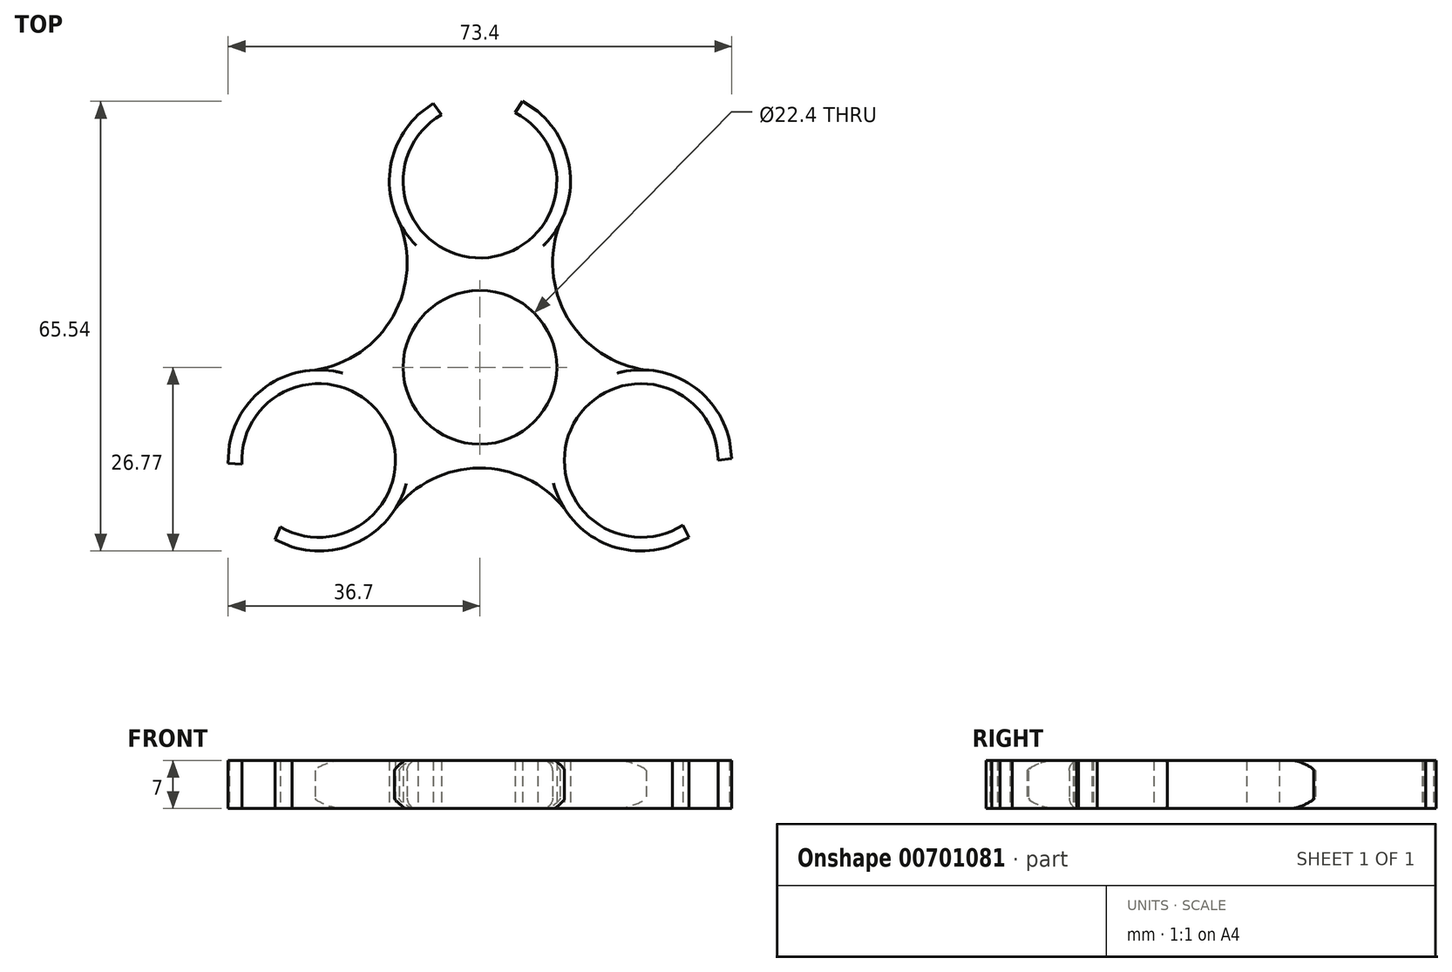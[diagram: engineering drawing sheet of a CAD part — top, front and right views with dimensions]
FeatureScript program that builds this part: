
annotation { "Feature Type Name" : "Feature", "Feature Type Description" : "" }
export const myFeature = defineFeature(function(context is Context, id is Id, definition is map)
    precondition{}
    {
        {
            var Q0;
            Q0=qCreatedBy(makeId("Top.planeOp"),FACE);
            var sketch = newSketch(context, id + "F0", { "sketchPlane" : qUnion([Q0])});
            skCircle(sketch, "E0", {"center": v(0, 0) * mm, "radius": 11.2 * mm});
            skArc(sketch, "E1", {"start": v(-6.82, 38.44) * mm, "mid": v(0.34, 13.94) * mm, "end": v(6.24, 38.77) * mm});
            skArc(sketch, "E2", {"start": v(-5.6, 36.83) * mm, "mid": v(0.28, 15.94) * mm, "end": v(5.12, 37.1) * mm});
            skArc(sketch, "E3.1.0", {"start": v(-29.1, -23.28) * mm, "mid": v(-13.95, -7.73) * mm, "end": v(-34.7, -14.12) * mm});
            skArc(sketch, "E3.1.1", {"start": v(-29.88, -25.13) * mm, "mid": v(-12.24, -6.68) * mm, "end": v(-36.7, -13.98) * mm});
            skArc(sketch, "E3.2.0", {"start": v(34.7, -13.56) * mm, "mid": v(13.67, -8.22) * mm, "end": v(29.57, -22.98) * mm});
            skArc(sketch, "E3.2.1", {"start": v(36.7, -13.31) * mm, "mid": v(11.9, -7.26) * mm, "end": v(30.46, -24.8) * mm});
            skLineSegment(sketch, "E4", {"start": v(6.24, 38.77) * mm, "end": v(8.44, 37.3) * mm});
            skLineSegment(sketch, "E5.1.0", {"start": v(-36.7, -13.98) * mm, "end": v(-36.51, -11.34) * mm});
            skLineSegment(sketch, "E5.2.0", {"start": v(30.46, -24.8) * mm, "end": v(28.08, -25.95) * mm});
            skLineSegment(sketch, "E6", {"start": v(-6.82, 38.44) * mm, "end": v(-9, 36.8) * mm});
            skLineSegment(sketch, "E7.1.0", {"start": v(-29.88, -25.13) * mm, "end": v(-27.36, -26.2) * mm});
            skLineSegment(sketch, "E7.2.0", {"start": v(36.7, -13.31) * mm, "end": v(36.36, -10.6) * mm});
            skArc(sketch, "E8", {"start": v(11.68, 20.99) * mm, "mid": v(12.77, 7.24) * mm, "end": v(24.25, -0.4) * mm});
            skArc(sketch, "E9.1.0", {"start": v(-24.01, -0.38) * mm, "mid": v(-12.66, 7.44) * mm, "end": v(-11.78, 21.2) * mm});
            skArc(sketch, "E9.2.0", {"start": v(12.34, -20.6) * mm, "mid": v(-0.11, -14.68) * mm, "end": v(-12.46, -20.8) * mm});
            skLineSegment(sketch, "E10", {"start": v(8.44, 37.3) * mm, "end": v(10.63, 30.66) * mm});
            skLineSegment(sketch, "E11", {"start": v(10.63, 30.66) * mm, "end": v(12.83, 24.03) * mm});
            skLineSegment(sketch, "E12", {"start": v(12.83, 24.03) * mm, "end": v(7.84, 19.14) * mm});
            skLineSegment(sketch, "E13", {"start": v(7.84, 19.14) * mm, "end": v(2.85, 14.25) * mm});
            skLineSegment(sketch, "E14", {"start": v(2.85, 14.25) * mm, "end": v(-3.74, 16.58) * mm});
            skLineSegment(sketch, "E15", {"start": v(-3.74, 16.58) * mm, "end": v(-10.32, 18.91) * mm});
            skLineSegment(sketch, "E16", {"start": v(-10.32, 18.91) * mm, "end": v(-10.91, 24.03) * mm});
            skLineSegment(sketch, "E17", {"start": v(-10.91, 24.03) * mm, "end": v(-13.1, 28.7) * mm});
            skLineSegment(sketch, "E18", {"start": v(-13.1, 28.7) * mm, "end": v(-8.74, 34.14) * mm});
            skLineSegment(sketch, "E19", {"start": v(-8.74, 34.14) * mm, "end": v(-6.82, 38.44) * mm});
            skLineSegment(sketch, "E20.1.0", {"start": v(-25.2, -24.64) * mm, "end": v(-29.88, -25.13) * mm});
            skLineSegment(sketch, "E20.1.1", {"start": v(-18.3, -25.7) * mm, "end": v(-25.2, -24.64) * mm});
            skLineSegment(sketch, "E20.1.2", {"start": v(-15.35, -21.47) * mm, "end": v(-18.3, -25.7) * mm});
            skLineSegment(sketch, "E20.1.3", {"start": v(-11.22, -18.4) * mm, "end": v(-15.35, -21.47) * mm});
            skLineSegment(sketch, "E20.1.4", {"start": v(-12.5, -11.53) * mm, "end": v(-11.22, -18.4) * mm});
            skLineSegment(sketch, "E20.1.5", {"start": v(-13.77, -4.66) * mm, "end": v(-12.5, -11.53) * mm});
            skLineSegment(sketch, "E20.1.6", {"start": v(-20.5, -2.78) * mm, "end": v(-13.77, -4.66) * mm});
            skLineSegment(sketch, "E20.1.7", {"start": v(-27.22, -0.9) * mm, "end": v(-20.5, -2.78) * mm});
            skLineSegment(sketch, "E20.1.8", {"start": v(-31.87, -6.12) * mm, "end": v(-27.22, -0.9) * mm});
            skLineSegment(sketch, "E20.1.9", {"start": v(-36.51, -11.34) * mm, "end": v(-31.87, -6.12) * mm});
            skLineSegment(sketch, "E20.2.0", {"start": v(33.94, -9.5) * mm, "end": v(36.7, -13.31) * mm});
            skLineSegment(sketch, "E20.2.1", {"start": v(31.4, -3) * mm, "end": v(33.94, -9.5) * mm});
            skLineSegment(sketch, "E20.2.2", {"start": v(26.27, -2.56) * mm, "end": v(31.4, -3) * mm});
            skLineSegment(sketch, "E20.2.3", {"start": v(21.54, -0.52) * mm, "end": v(26.27, -2.56) * mm});
            skLineSegment(sketch, "E20.2.4", {"start": v(16.23, -5.06) * mm, "end": v(21.54, -0.52) * mm});
            skLineSegment(sketch, "E20.2.5", {"start": v(10.92, -9.6) * mm, "end": v(16.23, -5.06) * mm});
            skLineSegment(sketch, "E20.2.6", {"start": v(12.66, -16.36) * mm, "end": v(10.92, -9.6) * mm});
            skLineSegment(sketch, "E20.2.7", {"start": v(14.4, -23.12) * mm, "end": v(12.66, -16.36) * mm});
            skLineSegment(sketch, "E20.2.8", {"start": v(21.24, -24.54) * mm, "end": v(14.4, -23.12) * mm});
            skLineSegment(sketch, "E20.2.9", {"start": v(28.08, -25.95) * mm, "end": v(21.24, -24.54) * mm});
            skLineSegment(sketch, "E21", {"start": v(-6.82, 38.44) * mm, "end": v(-5.6, 36.83) * mm});
            skLineSegment(sketch, "E22", {"start": v(6.24, 38.77) * mm, "end": v(5.12, 37.1) * mm});
            skLineSegment(sketch, "E23.1.0", {"start": v(-29.88, -25.13) * mm, "end": v(-29.1, -23.28) * mm});
            skLineSegment(sketch, "E23.1.1", {"start": v(-36.7, -13.98) * mm, "end": v(-34.7, -14.12) * mm});
            skLineSegment(sketch, "E23.2.0", {"start": v(36.7, -13.31) * mm, "end": v(34.7, -13.56) * mm});
            skLineSegment(sketch, "E23.2.1", {"start": v(30.46, -24.8) * mm, "end": v(29.57, -22.98) * mm});
            skSolve(sketch);
        }
        {
            var Q0;
            {var subQ0=sQuery(id+"F0.wireOp",EDGE,"E13");Q0=makeQuery(id+"F0.imprint","IMPRINT",FACE,{"disambiguationData":[TD([[makeQuery(id+"F0.imprint","IMPRINT",EDGE,{"derivedFrom":subQ0}),-1.0]])]});}
            var Q1;
            {var subQ0=sQuery(id+"F0.wireOp",EDGE,"E11");Q1=makeQuery(id+"F0.imprint","IMPRINT",FACE,{"disambiguationData":[TD([[makeQuery(id+"F0.imprint","IMPRINT",EDGE,{"derivedFrom":subQ0}),-1.0]])]});}
            var Q2;
            Q2=makeQuery(id+"F0.imprint","IMPRINT",FACE,{"disambiguationData":[TD([[makeQuery(id+"F0.imprint","IMPRINT",EDGE,{"derivedFrom":sQuery(id+"F0.wireOp",EDGE,"E4")}),-1.0]])]});
            var Q3;
            {var subQ0=sQuery(id+"F0.wireOp",EDGE,"E10");Q3=makeQuery(id+"F0.imprint","IMPRINT",FACE,{"disambiguationData":[TD([[makeQuery(id+"F0.imprint","IMPRINT",EDGE,{"derivedFrom":subQ0}),1.0]])]});}
            var Q4;
            {var subQ3=sQuery(id+"F0.wireOp",EDGE,"E12");Q4=makeQuery(id+"F0.imprint","IMPRINT",FACE,{"disambiguationData":[TD([[makeQuery(id+"F0.imprint","IMPRINT",EDGE,{"derivedFrom":subQ3}),1.0]])]});}
            var Q5;
            {var subQ0=sQuery(id+"F0.wireOp",EDGE,"E14");Q5=makeQuery(id+"F0.imprint","IMPRINT",FACE,{"disambiguationData":[TD([[makeQuery(id+"F0.imprint","IMPRINT",EDGE,{"derivedFrom":subQ0}),1.0]])]});}
            var Q6;
            {var subQ0=sQuery(id+"F0.wireOp",EDGE,"E6");Q6=makeQuery(id+"F0.imprint","IMPRINT",FACE,{"disambiguationData":[TD([[makeQuery(id+"F0.imprint","IMPRINT",EDGE,{"derivedFrom":subQ0}),1.0]])]});}
            var Q7;
            {var subQ0=sQuery(id+"F0.wireOp",EDGE,"E15");Q7=makeQuery(id+"F0.imprint","IMPRINT",FACE,{"disambiguationData":[TD([[makeQuery(id+"F0.imprint","IMPRINT",EDGE,{"derivedFrom":subQ0}),-1.0]])]});}
            var Q8;
            {var subQ3=sQuery(id+"F0.wireOp",EDGE,"E16");Q8=makeQuery(id+"F0.imprint","IMPRINT",FACE,{"disambiguationData":[TD([[makeQuery(id+"F0.imprint","IMPRINT",EDGE,{"derivedFrom":subQ3}),1.0]])]});}
            var Q9;
            Q9=makeQuery(id+"F0.imprint","IMPRINT",FACE,{"disambiguationData":[TD([[makeQuery(id+"F0.imprint","IMPRINT",EDGE,{"derivedFrom":sQuery(id+"F0.wireOp",EDGE,"E0")}),-1.0]])]});
            var Q10;
            {var subQ2=sQuery(id+"F0.wireOp",EDGE,"E20.1.6");Q10=makeQuery(id+"F0.imprint","IMPRINT",FACE,{"disambiguationData":[TD([[makeQuery(id+"F0.imprint","IMPRINT",EDGE,{"derivedFrom":subQ2}),1.0]])]});}
            var Q11;
            {var subQ0=sQuery(id+"F0.wireOp",EDGE,"E20.1.4");Q11=makeQuery(id+"F0.imprint","IMPRINT",FACE,{"disambiguationData":[TD([[makeQuery(id+"F0.imprint","IMPRINT",EDGE,{"derivedFrom":subQ0}),1.0]])]});}
            var Q12;
            {var subQ0=sQuery(id+"F0.wireOp",EDGE,"E20.1.5");Q12=makeQuery(id+"F0.imprint","IMPRINT",FACE,{"disambiguationData":[TD([[makeQuery(id+"F0.imprint","IMPRINT",EDGE,{"derivedFrom":subQ0}),-1.0]])]});}
            var Q13;
            {var subQ0=sQuery(id+"F0.wireOp",EDGE,"E20.1.1");Q13=makeQuery(id+"F0.imprint","IMPRINT",FACE,{"disambiguationData":[TD([[makeQuery(id+"F0.imprint","IMPRINT",EDGE,{"derivedFrom":subQ0}),-1.0]])]});}
            var Q14;
            {var subQ2=sQuery(id+"F0.wireOp",EDGE,"E20.1.2");Q14=makeQuery(id+"F0.imprint","IMPRINT",FACE,{"disambiguationData":[TD([[makeQuery(id+"F0.imprint","IMPRINT",EDGE,{"derivedFrom":subQ2}),1.0]])]});}
            var Q15;
            {var subQ0=sQuery(id+"F0.wireOp",EDGE,"E20.1.7");Q15=makeQuery(id+"F0.imprint","IMPRINT",FACE,{"disambiguationData":[TD([[makeQuery(id+"F0.imprint","IMPRINT",EDGE,{"derivedFrom":subQ0}),-1.0]])]});}
            var Q16;
            {var subQ2=sQuery(id+"F0.wireOp",EDGE,"E20.1.8");Q16=makeQuery(id+"F0.imprint","IMPRINT",FACE,{"disambiguationData":[TD([[makeQuery(id+"F0.imprint","IMPRINT",EDGE,{"derivedFrom":subQ2}),1.0]])]});}
            var Q17;
            Q17=makeQuery(id+"F0.imprint","IMPRINT",FACE,{"disambiguationData":[TD([[makeQuery(id+"F0.imprint","IMPRINT",EDGE,{"derivedFrom":sQuery(id+"F0.wireOp",EDGE,"E5.1.0")}),-1.0]])]});
            var Q18;
            {var subQ2=sQuery(id+"F0.wireOp",EDGE,"E20.1.0");Q18=makeQuery(id+"F0.imprint","IMPRINT",FACE,{"disambiguationData":[TD([[makeQuery(id+"F0.imprint","IMPRINT",EDGE,{"derivedFrom":subQ2}),-1.0]])]});}
            var Q19;
            {var subQ0=sQuery(id+"F0.wireOp",EDGE,"E7.1.0");Q19=makeQuery(id+"F0.imprint","IMPRINT",FACE,{"disambiguationData":[TD([[makeQuery(id+"F0.imprint","IMPRINT",EDGE,{"derivedFrom":subQ0}),1.0]])]});}
            var Q20;
            {var subQ0=sQuery(id+"F0.wireOp",EDGE,"E20.2.1");Q20=makeQuery(id+"F0.imprint","IMPRINT",FACE,{"disambiguationData":[TD([[makeQuery(id+"F0.imprint","IMPRINT",EDGE,{"derivedFrom":subQ0}),-1.0]])]});}
            var Q21;
            {var subQ0=sQuery(id+"F0.wireOp",EDGE,"E20.2.4");Q21=makeQuery(id+"F0.imprint","IMPRINT",FACE,{"disambiguationData":[TD([[makeQuery(id+"F0.imprint","IMPRINT",EDGE,{"derivedFrom":subQ0}),1.0]])]});}
            var Q22;
            {var subQ2=sQuery(id+"F0.wireOp",EDGE,"E20.2.2");Q22=makeQuery(id+"F0.imprint","IMPRINT",FACE,{"disambiguationData":[TD([[makeQuery(id+"F0.imprint","IMPRINT",EDGE,{"derivedFrom":subQ2}),1.0]])]});}
            var Q23;
            {var subQ0=sQuery(id+"F0.wireOp",EDGE,"E7.2.0");Q23=makeQuery(id+"F0.imprint","IMPRINT",FACE,{"disambiguationData":[TD([[makeQuery(id+"F0.imprint","IMPRINT",EDGE,{"derivedFrom":subQ0}),1.0]])]});}
            var Q24;
            {var subQ0=sQuery(id+"F0.wireOp",EDGE,"E20.2.5");Q24=makeQuery(id+"F0.imprint","IMPRINT",FACE,{"disambiguationData":[TD([[makeQuery(id+"F0.imprint","IMPRINT",EDGE,{"derivedFrom":subQ0}),-1.0]])]});}
            var Q25;
            {var subQ2=sQuery(id+"F0.wireOp",EDGE,"E20.2.6");Q25=makeQuery(id+"F0.imprint","IMPRINT",FACE,{"disambiguationData":[TD([[makeQuery(id+"F0.imprint","IMPRINT",EDGE,{"derivedFrom":subQ2}),1.0]])]});}
            var Q26;
            {var subQ0=sQuery(id+"F0.wireOp",EDGE,"E20.2.7");Q26=makeQuery(id+"F0.imprint","IMPRINT",FACE,{"disambiguationData":[TD([[makeQuery(id+"F0.imprint","IMPRINT",EDGE,{"derivedFrom":subQ0}),-1.0]])]});}
            var Q27;
            {var subQ2=sQuery(id+"F0.wireOp",EDGE,"E20.2.8");Q27=makeQuery(id+"F0.imprint","IMPRINT",FACE,{"disambiguationData":[TD([[makeQuery(id+"F0.imprint","IMPRINT",EDGE,{"derivedFrom":subQ2}),1.0]])]});}
            var Q28;
            Q28=makeQuery(id+"F0.imprint","IMPRINT",FACE,{"disambiguationData":[TD([[makeQuery(id+"F0.imprint","IMPRINT",EDGE,{"derivedFrom":sQuery(id+"F0.wireOp",EDGE,"E5.2.0")}),-1.0]])]});
            var Q29;
            {var subQ2=sQuery(id+"F0.wireOp",EDGE,"E20.2.0");Q29=makeQuery(id+"F0.imprint","IMPRINT",FACE,{"disambiguationData":[TD([[makeQuery(id+"F0.imprint","IMPRINT",EDGE,{"derivedFrom":subQ2}),-1.0]])]});}
            var Q30;
            {var subQ2=sQuery(id+"F0.wireOp",EDGE,"E19");Q30=makeQuery(id+"F0.imprint","IMPRINT",FACE,{"disambiguationData":[TD([[makeQuery(id+"F0.imprint","IMPRINT",EDGE,{"derivedFrom":subQ2}),-1.0]])]});}
            extrude(context, id + "F1", {"entities" : qUnion([Q0, Q1, Q2, Q3, Q4, Q5, Q6, Q7, Q8, Q9, Q10, Q11, Q12, Q13, Q14, Q15, Q16, Q17, Q18, Q19, Q20, Q21, Q22, Q23, Q24, Q25, Q26, Q27, Q28, Q29, Q30]), "depth" : 7 * mm, "offsetDistance" : 25 * mm});
        }
        {
            var Q0;
            Q0=makeQuery(id+"F1.opExtrude","CAP_EDGE",EDGE,{"disambiguationData":[OSD([sQuery(id+"F0.wireOp",EDGE,"E8")])],"isStart":false});
            var Q1;
            Q1=makeQuery(id+"F1.opExtrude","CAP_EDGE",EDGE,{"disambiguationData":[OSD([sQuery(id+"F0.wireOp",EDGE,"E8")])],"isStart":true});
            fillet(context, id + "F2", {"entities" : qUnion([Q0, Q1]), "radius" : 1.5 * mm, "tangentPropagation" : true, "allowEdgeOverflow" : false});
        }
        {
            var Q0;
            Q0=makeQuery(id+"F1.opExtrude","CAP_EDGE",EDGE,{"disambiguationData":[OSD([sQuery(id+"F0.wireOp",EDGE,"E9.1.0")])],"isStart":true});
            var Q1;
            Q1=makeQuery(id+"F1.opExtrude","CAP_EDGE",EDGE,{"disambiguationData":[OSD([sQuery(id+"F0.wireOp",EDGE,"E9.1.0")])],"isStart":false});
            fillet(context, id + "F3", {"entities" : qUnion([Q0, Q1]), "radius" : 1.5 * mm, "tangentPropagation" : true, "allowEdgeOverflow" : false});
        }
        {
            var Q0;
            Q0=makeQuery(id+"F1.opExtrude","CAP_EDGE",EDGE,{"disambiguationData":[OSD([sQuery(id+"F0.wireOp",EDGE,"E9.2.0")])],"isStart":true});
            var Q1;
            Q1=makeQuery(id+"F1.opExtrude","CAP_EDGE",EDGE,{"disambiguationData":[OSD([sQuery(id+"F0.wireOp",EDGE,"E9.2.0")])],"isStart":false});
            fillet(context, id + "F4", {"entities" : qUnion([Q0, Q1]), "radius" : 1.5 * mm, "tangentPropagation" : true, "allowEdgeOverflow" : false});
        }
    });
